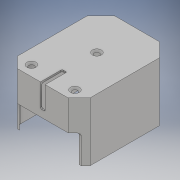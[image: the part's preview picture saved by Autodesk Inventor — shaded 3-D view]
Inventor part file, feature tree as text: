
AUTODESK INVENTOR PART (.ipt)
format: ipt  version: 2017 (Build 210142000, 142)  size: 257,536 bytes
history: native  units: mm
features: extrude x9, sketch x7, other x5, fillet x4, hole x3, projected_geometry x1
ambient origin geometry x8: Origin, YZ Plane, XZ Plane, XY Plane, X Axis, Y Axis, Z Axis, Center Point
bodies: Body1 (feature_tree)
feature tree (29):
  other  "Твердое тело1"
  sketch  "Эскиз1"
  extrude  "Выдавливание1"  Depth=58.6mm
  extrude  "Выдавливание2"  Depth=77.0mm
  fillet  "Сопряжение1"  Radius=11.0mm
  extrude  "Выдавливание3"  Depth=11.0mm
  extrude  "Выдавливание4"  Depth=8.5mm
  extrude  "Выдавливание5"  Depth=8.5mm
  other  "Комбинировать1"
  hole  "Отверстие4"  [1 undecoded]
  hole  "Отверстие5"  [1 undecoded]
  hole  "Отверстие6"  [1 undecoded]
  fillet  "Сопряжение2"  Radius=11.0mm
  fillet  "Сопряжение3"  Radius=1.2mm
  extrude  "Выдавливание6"  Depth=1.5mm TaperAngle=0.0deg
  extrude  "Выдавливание7"  Depth=48.0mm TaperAngle=0.0deg
  extrude  "Выдавливание8"  Depth=1.0mm
  other  "Комбинировать2"
  fillet  "Сопряжение4"  Radius=4.0mm
  extrude  "Выдавливание11"  Depth=17.0mm
  other  "Твердое тело2"
  sketch  "Эскиз2"
  sketch  "Эскиз3"
  sketch  "Эскиз4"
  other  "Твердое тело3"
  sketch  "Эскиз5"
  sketch  "Эскиз6"
  sketch  "Эскиз9"
  projected_geometry  "Спроецированная петля1"
note: 3 required parameter values undecoded (feature->parameter linkage not recoverable at this tier; creation-order binding heuristic only, values carry confidence <= 0.55)
